# Revit family: QF_GIORIK_SEME202W_SEPE202W_SETE202W_SEHE202W
name_source: partatom
category: Specialty Equipment
revit_build: Autodesk Revit 2014 (Build: 20140709_2115(x64)
units: mm (PartAtom-declared; Revit-internal decimal feet)

## types (4) — shared parameters
Assembly Code = E1090320
Cold Water Connection Height = 188 mm
Cold Water Size = 1"
Cold Water Temperature Recommended = 0 °C
Cycle = 50 Hz
FL Amps = 0 A
HP = 0
Indirect Waste Connection Height = 149 mm
Indirect Waste Flow = 0.0 L/s
Indirect Waste Size = 2"
Manufacturer = GIORIK
Max Overcurrent Protection = 20 A
Min Ckt Ampacity = 0 A
Phase = 3
URL = www.giorik.com
Volts = 400 V
Waste Water Discharge Temperature = 0 °C
Weight in Pounds = 815.71

## per-type parameters (varying)
| type | Apparent Power | Description | Digital control | Touch screen control | Watts |
| SEME202W | 51600 VA | ELECTRIC OVEN 20 GN 2/1 COMBINED CONVECTION/STEAM DIGITAL CONTROL BOARD - WITH HIGH EFFICIENCY BOILER | Yes | No | 51600 W |
| SEPE202W | 51600 VA | ELECTRIC OVEN 20 GN 2/1 COMBINED CONVECTION/STEAM DIGITAL CONTROL | Yes | No | 51600 W |
| SEHE202W | 54100 VA | ELECTRIC OVEN 20 GN 2/1 COMBINED CONVECTION/STEAM TOUCH SCREEN CONTROL - WITH HIGH EFFICIENCY BOILER | No | Yes | 54100 W |
| SETE202W | 51600 VA | ELECTRIC OVEN 20 GN 2/1 COMBINED CONVECTION/STEAM TOUCH SCREEN CONTROL | No | Yes | 51600 W |

note: column(s) folded — value = type name in every type: Model

## geometry (parser evidence)
native form markers: Blend x2, Sweep x2
no freeform markers — native parametric forms only
